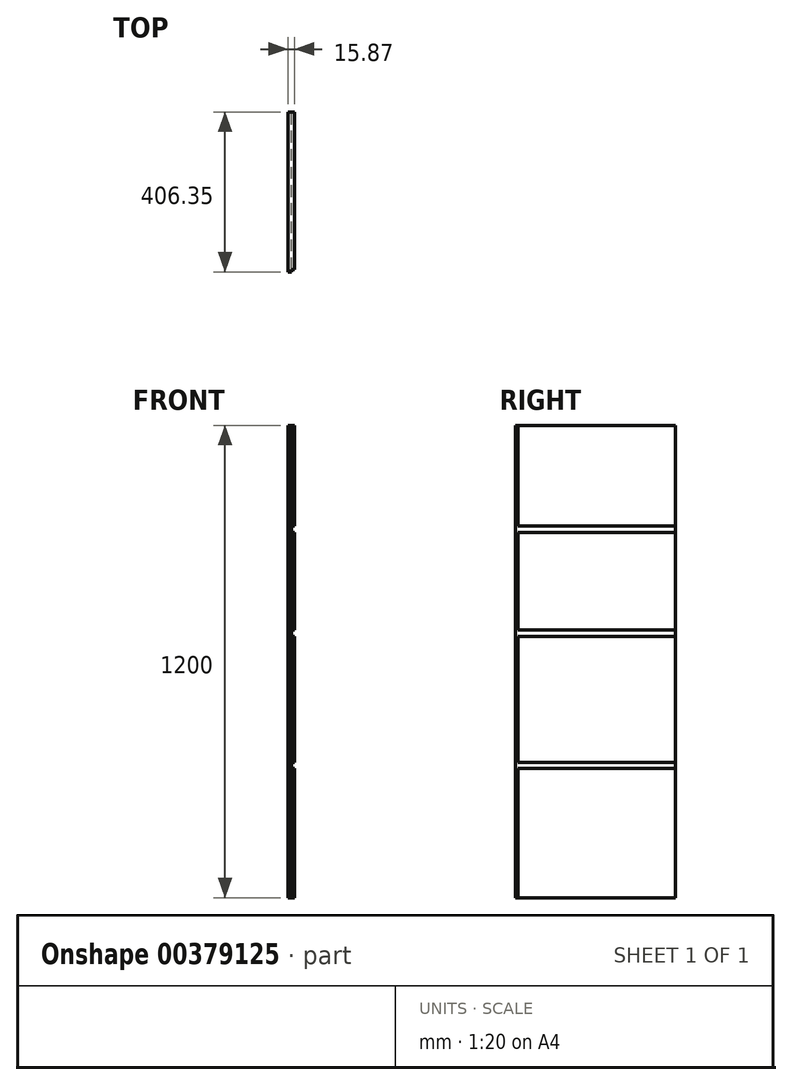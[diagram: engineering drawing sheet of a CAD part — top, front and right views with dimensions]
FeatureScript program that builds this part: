
annotation { "Feature Type Name" : "Feature", "Feature Type Description" : "" }
export const myFeature = defineFeature(function(context is Context, id is Id, definition is map)
    precondition{}
    {
        {
            var Q0;
            Q0=qCreatedBy(makeId("Front.planeOp"),FACE);
            var sketch = newSketch(context, id + "F0", { "sketchPlane" : qUnion([Q0])});
            skLineSegment(sketch, "E0.bottom", {"start": v(-45.4, 967.8) * mm, "end": v(-29.52, 967.8) * mm});
            skLineSegment(sketch, "E0.top", {"start": v(-45.4, -232.2) * mm, "end": v(-29.52, -232.2) * mm});
            skLineSegment(sketch, "E0.left", {"start": v(-45.4, 967.8) * mm, "end": v(-45.4, -232.2) * mm});
            skLineSegment(sketch, "E0.right", {"start": v(-29.52, 967.8) * mm, "end": v(-29.52, -232.2) * mm});
            skLineSegment(sketch, "E1.bottom", {"start": v(-29.52, 111.6) * mm, "end": v(-37.46, 111.6) * mm});
            skLineSegment(sketch, "E1.top", {"start": v(-29.52, 95.73) * mm, "end": v(-37.46, 95.73) * mm});
            skLineSegment(sketch, "E1.left", {"start": v(-29.52, 111.6) * mm, "end": v(-29.52, 95.73) * mm});
            skLineSegment(sketch, "E1.right", {"start": v(-37.46, 111.6) * mm, "end": v(-37.46, 95.73) * mm});
            skLineSegment(sketch, "E2.bottom", {"start": v(-29.52, 431.6) * mm, "end": v(-37.46, 431.6) * mm});
            skLineSegment(sketch, "E2.top", {"start": v(-29.52, 447.48) * mm, "end": v(-37.46, 447.48) * mm});
            skLineSegment(sketch, "E2.left", {"start": v(-29.52, 431.6) * mm, "end": v(-29.52, 447.48) * mm});
            skLineSegment(sketch, "E2.right", {"start": v(-37.46, 431.6) * mm, "end": v(-37.46, 447.48) * mm});
            skLineSegment(sketch, "E3.bottom", {"start": v(-29.52, 695.73) * mm, "end": v(-37.46, 695.73) * mm});
            skLineSegment(sketch, "E3.top", {"start": v(-29.52, 711.6) * mm, "end": v(-37.46, 711.6) * mm});
            skLineSegment(sketch, "E3.left", {"start": v(-29.52, 695.73) * mm, "end": v(-29.52, 711.6) * mm});
            skLineSegment(sketch, "E3.right", {"start": v(-37.46, 695.73) * mm, "end": v(-37.46, 711.6) * mm});
            skSolve(sketch);
        }
        {
            var Q0;
            {var subQ10=sQuery(id+"F0.wireOp",EDGE,"E0.bottom");Q0=makeQuery(id+"F0.imprint","IMPRINT",FACE,{"disambiguationData":[TD([[makeQuery(id+"F0.imprint","IMPRINT",EDGE,{"derivedFrom":subQ10}),-1.0]])]});}
            extrude(context, id + "F1", {"entities" : qUnion([Q0]), "depth" : 406.35 * mm});
        }
        {
            var Q0;
            Q0=makeQuery(id+"F1.opExtrude","SWEPT_FACE",FACE,{"disambiguationData":[OSD([sQuery(id+"F0.wireOp",EDGE,"E0.bottom")])]});
            var sketch = newSketch(context, id + "F2", { "sketchPlane" : qUnion([Q0])});
            skLineSegment(sketch, "E4.bottom", {"start": v(-29.52, -406.35) * mm, "end": v(-37.46, -406.35) * mm});
            skLineSegment(sketch, "E4.top", {"start": v(-29.52, -400) * mm, "end": v(-37.46, -400) * mm});
            skLineSegment(sketch, "E4.left", {"start": v(-29.52, -406.35) * mm, "end": v(-29.52, -400) * mm});
            skLineSegment(sketch, "E4.right", {"start": v(-37.46, -406.35) * mm, "end": v(-37.46, -400) * mm});
            skSolve(sketch);
        }
        {
            var Q0;
            Q0=makeQuery(id+"F2.imprint","IMPRINT",FACE,{"disambiguationData":[TD([[makeQuery(id+"F2.imprint","IMPRINT",EDGE,{"derivedFrom":sQuery(id+"F2.wireOp",EDGE,"PIznmBNc-6bbk-rZ0Q-YaKz-bY3aFbiOntty.bottom")}),-1.0]])]});
            var Q1;
            Q1=makeQuery(id+"F2.imprint","IMPRINT",FACE,{"disambiguationData":[TD([[makeQuery(id+"F2.imprint","IMPRINT",EDGE,{"derivedFrom":sQuery(id+"F2.wireOp",EDGE,"E4.bottom")}),1.0]])]});
            extrude(context, id + "F3", {"entities" : qUnion([Q0, Q1]), "operationType" : NewBodyOperationType.REMOVE, "endBound" : BoundingType.THROUGH_ALL, "oppositeDirection" : true, "depth" : 25 * mm});
        }
    });
